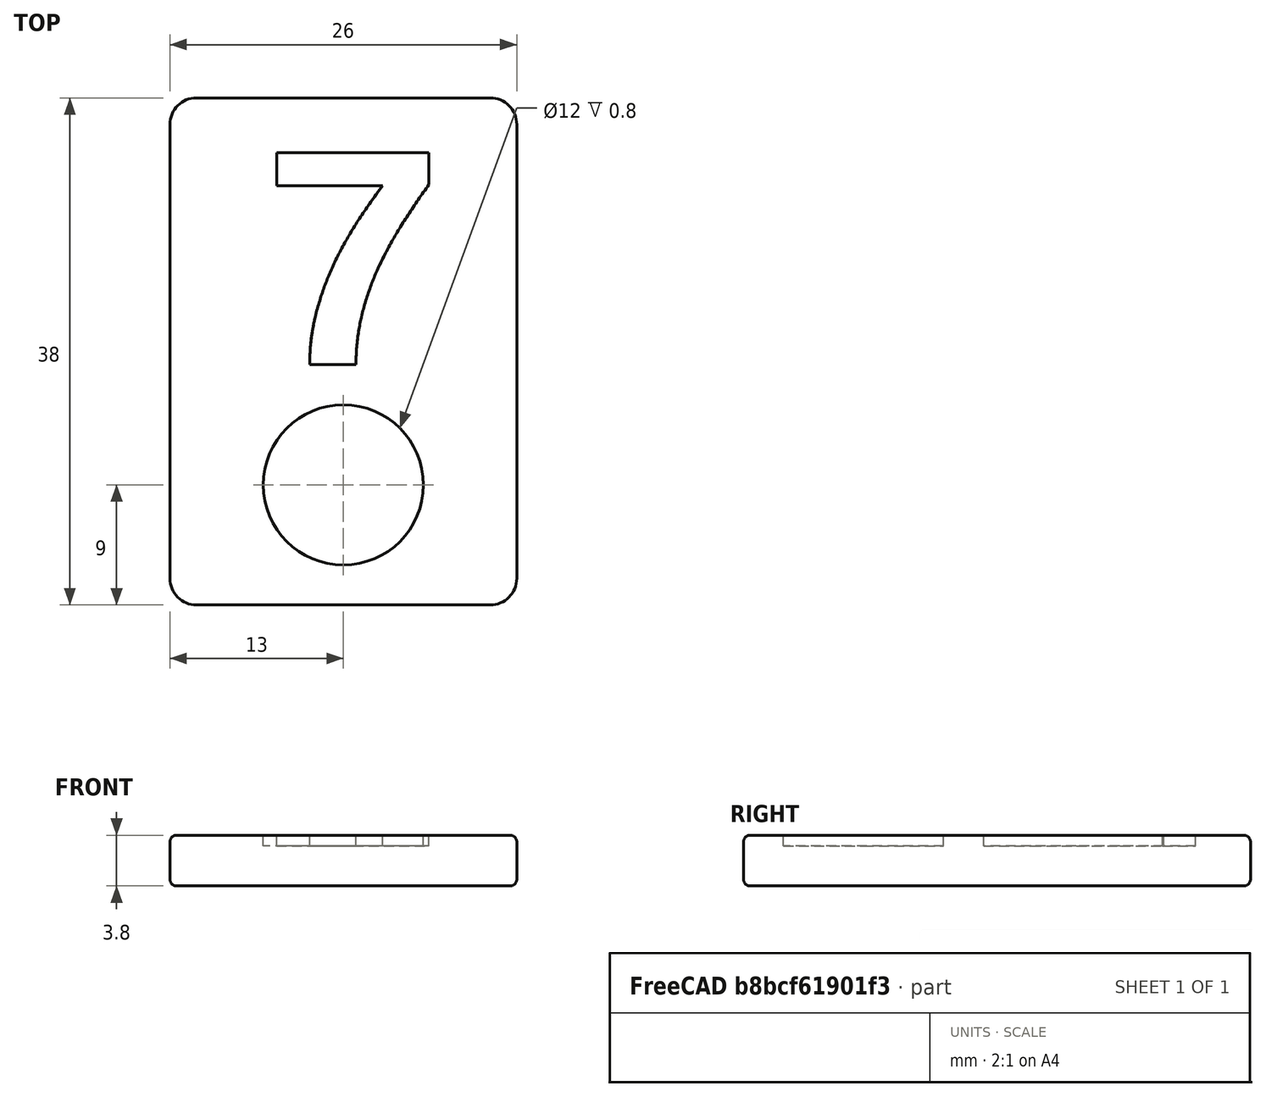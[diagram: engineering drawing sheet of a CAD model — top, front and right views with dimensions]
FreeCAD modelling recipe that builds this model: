
FCSTD DOCUMENT  (FreeCAD 0.14R3702 (Git))
Label: ficha_carmen4
License: CC-BY 3.0
LicenseURL: http://creativecommons.org/licenses/by/3.0/
objects: Part::Cut×2, Part::Part2DObjectPython×1, Part::Cylinder×1, Part::Extrusion×1, Part::Fillet×1, App::DocumentObjectGroup×1
note: 6 computed .brp shape members not serialized (recipe doc carries the construction recipe); baked Part::Feature solids carry a one-line shape summary decoded from their .brp

FEATURE [Part::Part2DObjectPython] ShapeString  # Draft 2D object (typed FeaturePython)
  FontFile = <path>
  Placement = pos=(6.5,18,4) rot=(0,0,1;0rad)
  Size = 18
  String = 9
  Tracking = 0
FEATURE [Part::Cylinder] Cylinder  label="Cilindro"
  Angle = 360
  Height = 10
  Placement = pos=(13,9,3) rot=(0,0,1;0rad)
  Radius = 6
FEATURE [Part::Extrusion] Extrude
  Base = -> ShapeString
  Dir = (0,0,2)
  Placement = pos=(0,0,-1) rot=(0,0,1;0rad)
  Solid = true
FEATURE [Part::Cut] Cut003
  Tool = -> Cylinder
FEATURE [Part::Cut] Cut002
  Base = -> Cut003
  Tool = -> Extrude
FEATURE [Part::Fillet] Fillet001  label="rummy9"
  Base = -> Cut002
  Edges = 16 edges r=0.5: [Edge1,Edge4,Edge20,Edge21,Edge22,Edge23,Edge24,Edge25,Edge26,Edge27,Edge29,Edge31,Edge32,Edge33,Edge34,Edge35]
FEATURE [App::DocumentObjectGroup] Grupo
  Group = -> [Fillet001]
note: 1 file-system path scrubbed to <path> (originals preserved in the JSON sidecar)
